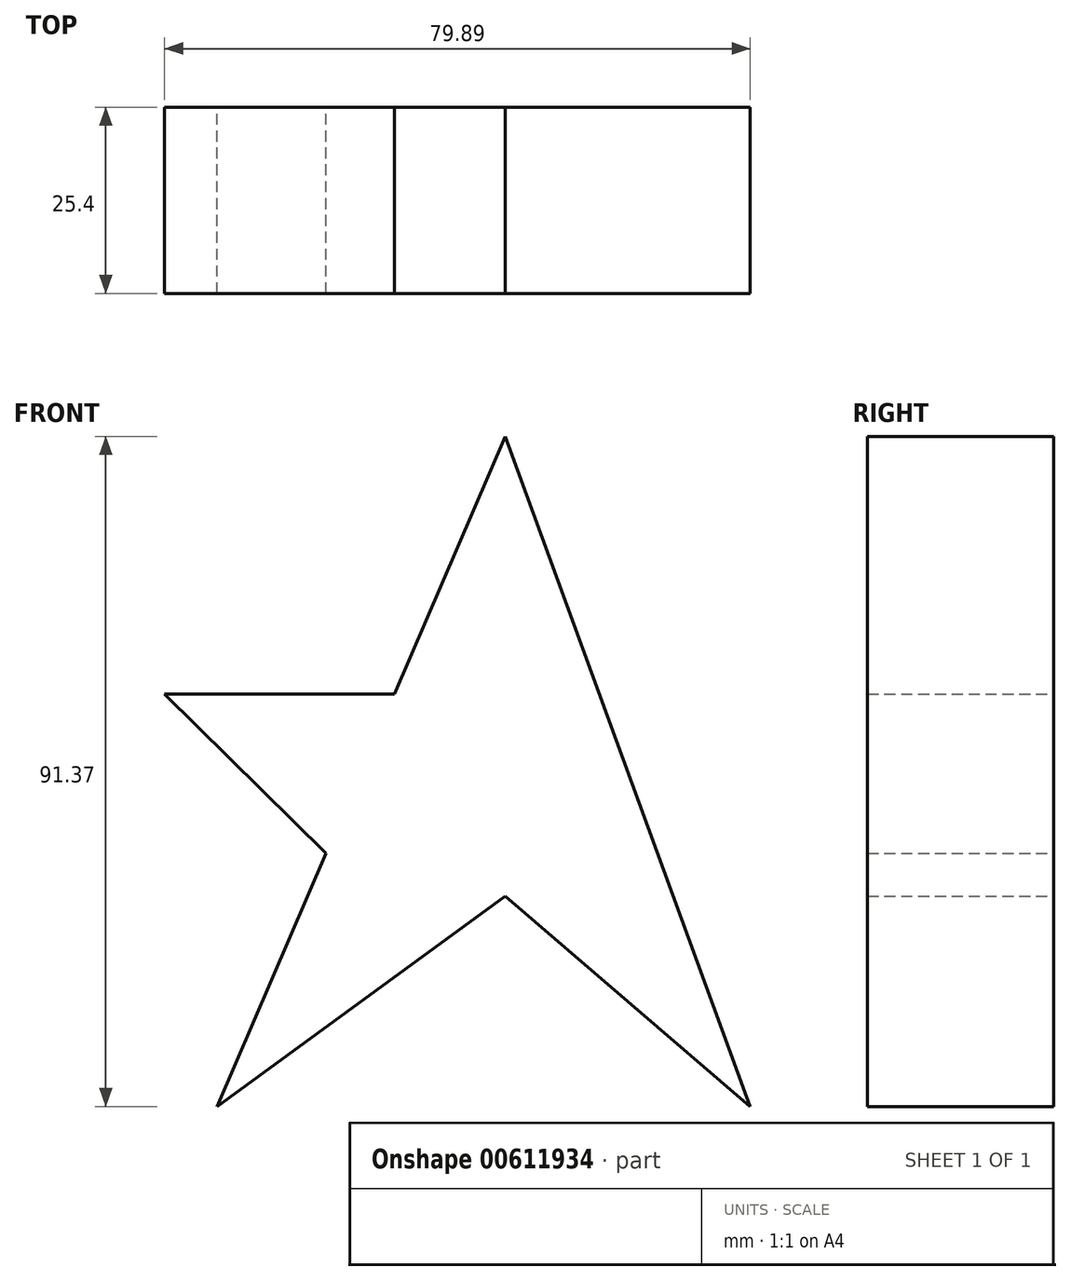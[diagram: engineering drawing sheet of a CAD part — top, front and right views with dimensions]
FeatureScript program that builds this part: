
annotation { "Feature Type Name" : "Feature", "Feature Type Description" : "" }
export const myFeature = defineFeature(function(context is Context, id is Id, definition is map)
    precondition{}
    {
        {
            var Q0;
            Q0=qCreatedBy(makeId("Front.planeOp"),FACE);
            var sketch = newSketch(context, id + "F0", { "sketchPlane" : qUnion([Q0])});
            skLineSegment(sketch, "E0", {"start": v(0, 0) * mm, "end": v(0, 35.15) * mm});
            skLineSegment(sketch, "E1", {"start": v(0, 35.15) * mm, "end": v(-39.28, -56.22) * mm});
            skLineSegment(sketch, "E2", {"start": v(-39.28, -56.22) * mm, "end": v(0, -27.51) * mm});
            skLineSegment(sketch, "E3", {"start": v(0, -27.51) * mm, "end": v(33.43, -56.22) * mm});
            skLineSegment(sketch, "E4", {"start": v(33.43, -56.22) * mm, "end": v(0, 35.15) * mm});
            skLineSegment(sketch, "E5", {"start": v(-15.11, 0) * mm, "end": v(-46.46, 0) * mm});
            skLineSegment(sketch, "E6", {"start": v(-46.46, 0) * mm, "end": v(-24.45, -21.71) * mm});
            skLineSegment(sketch, "E7", {"start": v(41.08, 0) * mm, "end": v(20.8, -21.71) * mm});
            skLineSegment(sketch, "E8", {"start": v(20.8, -21.71) * mm, "end": v(41.08, 0) * mm});
            skLineSegment(sketch, "E9", {"start": v(41.08, 0) * mm, "end": v(12.86, 0) * mm});
            skSolve(sketch);
        }
        {
            var Q0;
            {var subQ0=sQuery(id+"F0.wireOp",EDGE,"E2");Q0=makeQuery(id+"F0.imprint","IMPRINT",FACE,{"disambiguationData":[TD([[makeQuery(id+"F0.imprint","IMPRINT",EDGE,{"derivedFrom":subQ0}),1.0]])]});}
            var Q1;
            {var subQ0=sQuery(id+"F0.wireOp",EDGE,"E8");Q1=makeQuery(id+"F0.imprint","IMPRINT",FACE,{"disambiguationData":[TD([[makeQuery(id+"F0.imprint","IMPRINT",EDGE,{"derivedFrom":subQ0}),1.0]])]});}
            var Q2;
            {var subQ0=sQuery(id+"F0.wireOp",EDGE,"E5");Q2=makeQuery(id+"F0.imprint","IMPRINT",FACE,{"disambiguationData":[TD([[makeQuery(id+"F0.imprint","IMPRINT",EDGE,{"derivedFrom":subQ0}),1.0]])]});}
            extrude(context, id + "F1", {"entities" : qUnion([Q0, Q1, Q2]), "depth" : 25.4 * mm, "offsetDistance" : 25.4 * mm});
        }
    });
